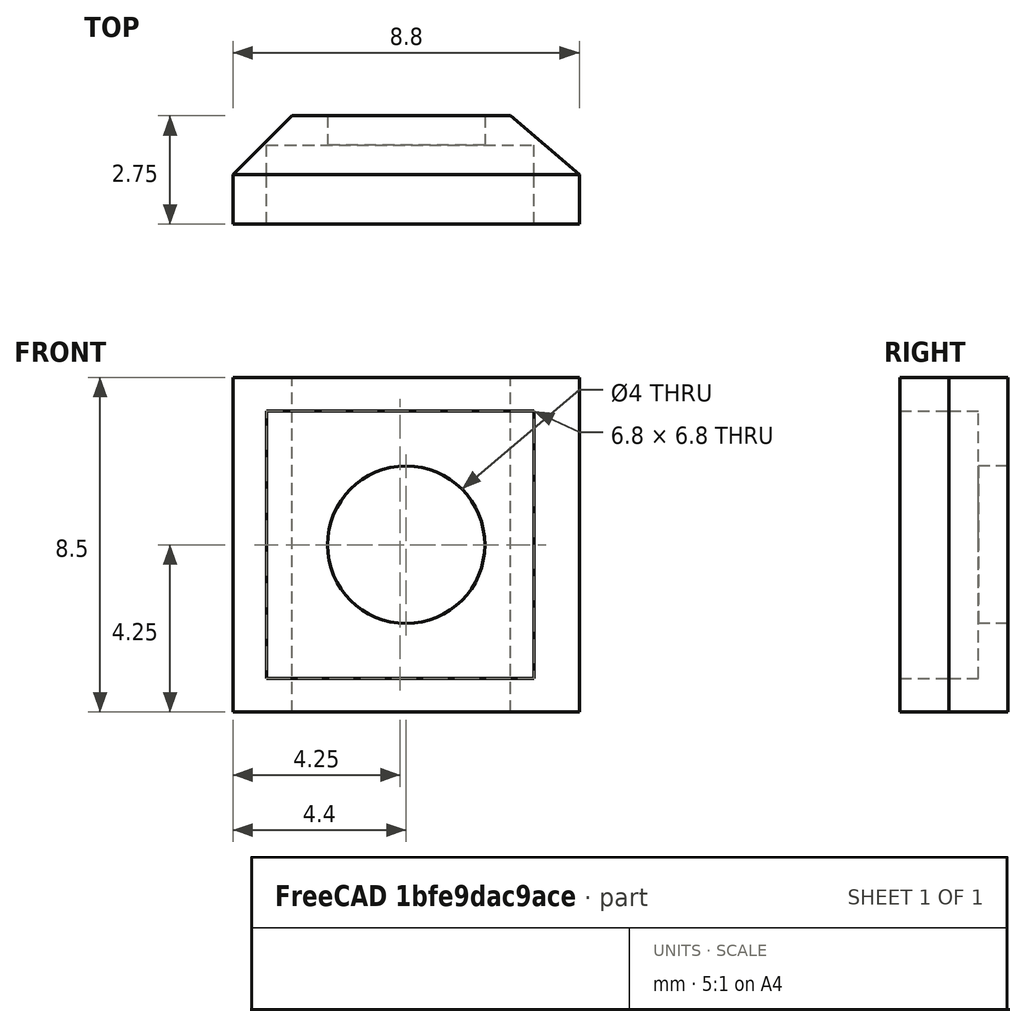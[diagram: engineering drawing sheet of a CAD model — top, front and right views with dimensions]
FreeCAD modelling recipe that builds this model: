
FCSTD DOCUMENT  (FreeCAD 0.19R24276 (Git))
Label: T-hold_mini_002
License: All rights reserved
LicenseURL: http://en.wikipedia.org/wiki/All_rights_reserved
objects: Part::Cut×5, Part::Cylinder×3, Part::Box×3, Part::Wedge×1, Part::Compound×1, Mesh::Feature×1
note: 13 computed .brp shape members not serialized (recipe doc carries the construction recipe); baked Part::Feature solids carry a one-line shape summary decoded from their .brp

FEATURE [Part::Cylinder] Cylinder004  label="Válec004"
  Angle = 360
  AttacherType = Attacher::AttachEngine3D
  Height = 10
  Placement = pos=(4.4,5,4.25) rot=(1,0,0;1.5708rad)
  Radius = 2
FEATURE [Part::Cylinder] Cylinder003  label="Válec003"
  Angle = 360
  AttacherType = Attacher::AttachEngine3D
  Height = 10
  Placement = pos=(4.4,5,4.25) rot=(1,0,0;1.5708rad)
  Radius = 2
FEATURE [Part::Box] Box003  label="Krychle003"
  AttacherType = Attacher::AttachEngine3D
  Height = 6.8
  Length = 6.8
  Placement = pos=(0.85,-1.25,0.85) rot=(0,0,1;0rad)
  Width = 2
FEATURE [Part::Cylinder] Cylinder005  label="Válec005"
  Angle = 360
  AttacherType = Attacher::AttachEngine3D
  Height = 10
  Placement = pos=(4.4,5,4.25) rot=(1,0,0;1.5708rad)
  Radius = 2
FEATURE [Part::Box] Box005  label="Krychle005"
  AttacherType = Attacher::AttachEngine3D
  Height = 6.8
  Length = 6.8
  Placement = pos=(0.85,-1.5,0.85) rot=(0,0,1;0rad)
  Width = 2
FEATURE [Part::Box] Box004  label="Krychle004"
  AttacherType = Attacher::AttachEngine3D
  Height = 8.5
  Length = 8.8
  Placement = pos=(0,-1.5,0) rot=(0,0,1;0rad)
  Width = 1.25
FEATURE [Part::Cut] Cut007
  Base = -> Box004
  Tool = -> Box005
FEATURE [Part::Cut] Cut006
  Base = -> Cut007
  Tool = -> Cylinder004
FEATURE [Part::Cut] Cut009
  Base = -> Cut006
  Placement = pos=(0,0.25,0) rot=(0,0,1;0rad)
  Tool = -> Cylinder003
FEATURE [Part::Wedge] Wedge001  label="Klín001"
  AttacherType = Attacher::AttachEngine3D
  X2max = 7.05
  X2min = 1.5
  Xmax = 8.8
  Xmin = 0
  Ymax = 1.5
  Ymin = 0
  Z2max = 8.5
  Z2min = 0
  Zmax = 8.5
  Zmin = 0
FEATURE [Part::Cut] Cut008
  Base = -> Wedge001
  Tool = -> Box003
FEATURE [Part::Compound] Compound001  label="teckovka001"
  Links = -> [Cut008,Cut009]
FEATURE [Part::Cut] Cut005  label="T-hold_mini"
  Base = -> Compound001
  Tool = -> Cylinder005
FEATURE [Mesh::Feature] Mesh  label="T-hold_mini (Meshed)"
